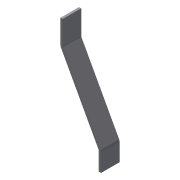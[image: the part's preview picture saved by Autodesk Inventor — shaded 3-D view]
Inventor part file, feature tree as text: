
AUTODESK INVENTOR PART (.ipt)
format: ipt  version: 2015 (Build 190159000, 159)  size: 164,864 bytes
history: native  units: in
note: dims shown in document units (in); Inventor stores cm internally (conversion verified against a paired STEP export)
features: reference x10, other x4, sheet_metal_op x3, sketch x3, hole x1
ambient origin geometry x8: Origin, YZ Plane, XZ Plane, XY Plane, X Axis, Y Axis, Z Axis, Center Point
bodies: Body1 (feature_tree)
feature tree (21):
  sheet_metal_op  "Contour Flange2"
  hole  "Hole1"  [1 undecoded]
  other  "A-Side Definition"
  sketch  "Sketch2"  dims[d10=0.12in d11=0.06in]
  other  "Plate2"
  sheet_metal_op  "Bend2"
  sheet_metal_op  "Corner2"
  reference  "Reference3"
  reference  "Reference4"
  reference  "Reference5"
  reference  "Reference6"
  reference  "Reference7"
  sketch  "Sketch3"  dims[d12=0.24in]
  reference  "Reference8"
  reference  "Reference9"
  reference  "Reference10"
  reference  "Reference11"
  sketch  "Sketch4"  dims[d13=0.12in d14=1.0in d15=0.12in d16=0.12in d17=0.48in d18=0.12in d19=0.12in d20=1.0in d21=0.25in d22=0.25in d23=0.75in d24=0.375in d25=0.25in d26=0.5635in d27=12.0in d28=0.0in d29=0.12in d30=0.0in]
  reference  "Reference12"
  other  "Cut1"
  other  "Definition1"
note: 1 required parameter value undecoded (feature->parameter linkage not recoverable at this tier; creation-order binding heuristic only, values carry confidence <= 0.55)
